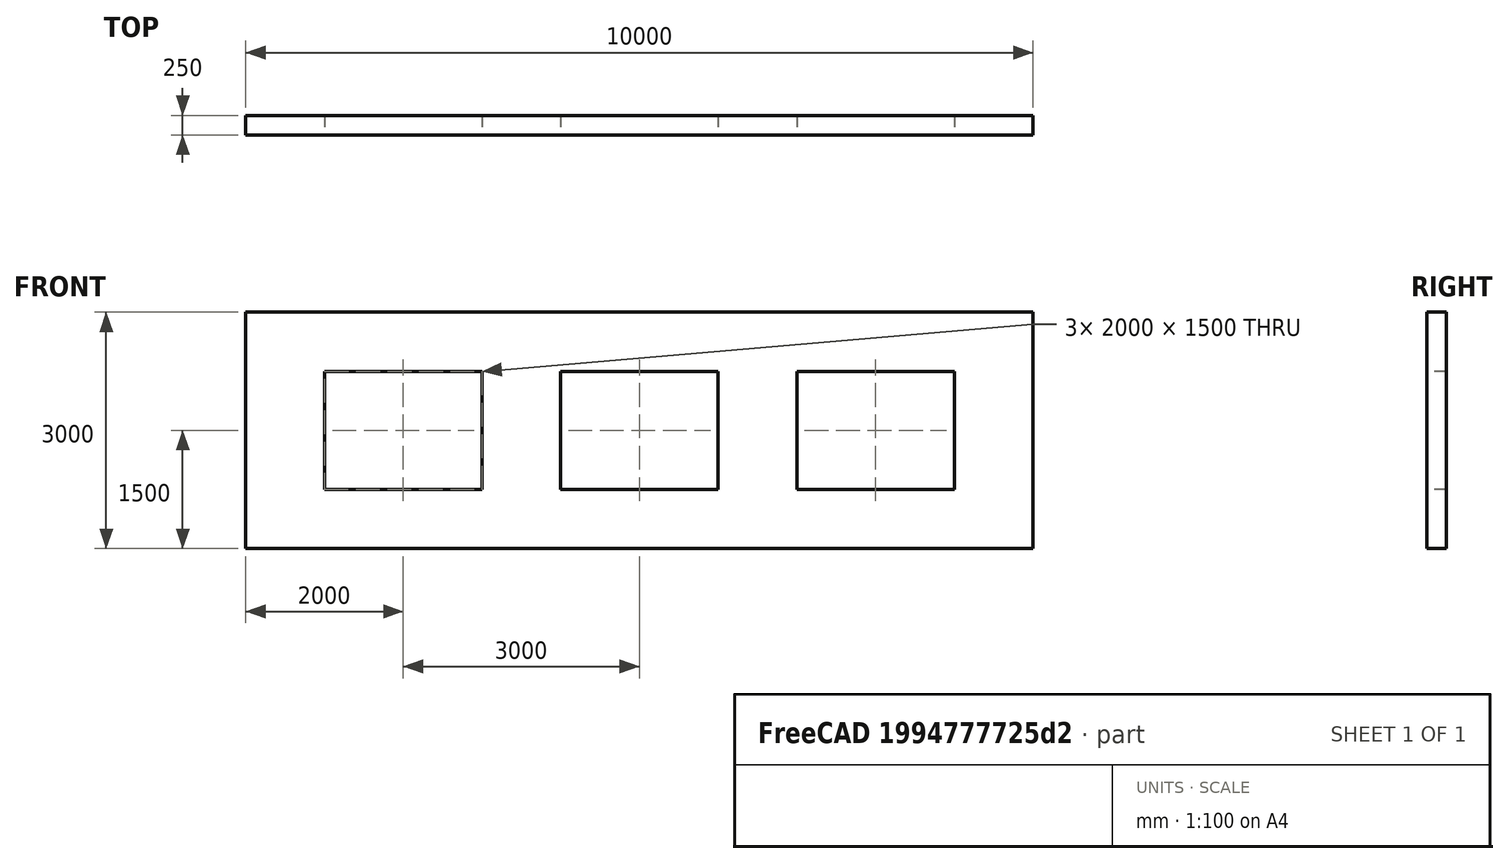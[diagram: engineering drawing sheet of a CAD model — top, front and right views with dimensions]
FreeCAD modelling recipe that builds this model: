
FCSTD DOCUMENT  (FreeCAD 0.21R33694 (Git))
Label: wall_with_openings
License: All rights reserved
LicenseURL: http://en.wikipedia.org/wiki/All_rights_reserved
objects: Part::Box×1, Sketcher::SketchObject×1, Part::Extrusion×1, Part::Cut×1, Fem::ConstraintFixed×1, App::MaterialObjectPython×1, Fem::ConstraintForce×1, Fem::FemSolverObjectPython×1, Fem::FemMeshObjectPython×1, Fem::FemAnalysis×1
note: 4 computed .brp shape members not serialized (recipe doc carries the construction recipe); baked Part::Feature solids carry a one-line shape summary decoded from their .brp

FEATURE [Part::Box] Box  label="Cube"
  AttacherType = Attacher::AttachEngine3D
  Height = 3000
  Length = 10000
  Width = 250
FEATURE [Sketcher::SketchObject] Sketch
  FullyConstrained = true
  MapMode = 5
  Placement = pos=(0,0,0) rot=(1,0,0;1.5708rad)
  Support = -> [Box]
  sketch-geometry (12):
    g0: LineSegment StartX=1000 StartY=750 StartZ=0 EndX=3000 EndY=750 EndZ=0
    g1: LineSegment StartX=3000 StartY=750 StartZ=0 EndX=3000 EndY=2250 EndZ=0
    g2: LineSegment StartX=3000 StartY=2250 StartZ=0 EndX=1000 EndY=2250 EndZ=0
    g3: LineSegment StartX=1000 StartY=2250 StartZ=0 EndX=1000 EndY=750 EndZ=0
    g4: LineSegment StartX=4000 StartY=750 StartZ=0 EndX=6000 EndY=750 EndZ=0
    g5: LineSegment StartX=6000 StartY=750 StartZ=0 EndX=6000 EndY=2250 EndZ=0
    g6: LineSegment StartX=6000 StartY=2250 StartZ=0 EndX=4000 EndY=2250 EndZ=0
    g7: LineSegment StartX=4000 StartY=2250 StartZ=0 EndX=4000 EndY=750 EndZ=0
    g8: LineSegment StartX=7000 StartY=750 StartZ=0 EndX=9000 EndY=750 EndZ=0
    g9: LineSegment StartX=9000 StartY=750 StartZ=0 EndX=9000 EndY=2250 EndZ=0
    g10: LineSegment StartX=9000 StartY=2250 StartZ=0 EndX=7000 EndY=2250 EndZ=0
    g11: LineSegment StartX=7000 StartY=2250 StartZ=0 EndX=7000 EndY=750 EndZ=0
  constraints (36):
    c: Coincident(g0,g1)
    c: Coincident(g1,g2)
    c: Coincident(g2,g3)
    c: Coincident(g3,g0)
    c: Horizontal(g0)
    c: Horizontal(g2)
    c: Vertical(g1)
    c: Vertical(g3)
    c: Coincident(g4,g5)
    c: Coincident(g5,g6)
    c: Coincident(g6,g7)
    c: Coincident(g7,g4)
    c: Horizontal(g4)
    c: Horizontal(g6)
    c: Vertical(g5)
    c: Vertical(g7)
    c: Coincident(g8,g9)
    c: Coincident(g9,g10)
    c: Coincident(g10,g11)
    c: Coincident(g11,g8)
    c: Horizontal(g8)
    c: Horizontal(g10)
    c: Vertical(g9)
    c: Vertical(g11)
    c: DistanceY(g3,g3) = 1500
    c: DistanceY(g7,g7) = 1500
    c: DistanceY(g11,g11) = 1500
    c: DistanceY(g-1,g0) = 750
    c: DistanceY(g-1,g4) = 750
    c: DistanceY(g-1,g8) = 750
    c: DistanceX(g0,g0) = 2000
    c: DistanceX(g4,g4) = 2000
    c: DistanceX(g8,g8) = 2000
    c: DistanceX(g1,g6) = 1000
    c: DistanceX(g5,g10) = 1000
    c: DistanceX(g-1,g0) = 1000
FEATURE [Part::Extrusion] Extrude
  Base = -> Sketch
  Dir = (0,-1,2e-16)
  DirMode = 2
  FaceMakerClass = Part::FaceMakerBullseye
  LengthFwd = 0
  LengthRev = 350
  Solid = true
  Symmetric = false
FEATURE [Part::Cut] Cut
  Base = -> Box
  Tool = -> Extrude
FEATURE [Fem::ConstraintFixed] ConstraintFixed
  NormalDirection = (-1,0,0)
  Normals = (72) [(-1,0,0),(-1,0,0),(-1,0,0),(-1,0,0),(-1,0,0),(-1,0,0),(-1,0,0),(-1,0,0),(-1,0,0),(-1,0,0),(-1,0,0),(-1,0,0),(-1,0,0),(-1,0,0),(-1,0,0),(-1,0,0),+56 more]
  Points = (72) [(0,250,0),(0,250,375),(0,250,750),(0,250,1125),(0,250,1500),(0,250,1875),(0,250,2250),(0,250,2625),(0,250,3000),(0,166.667,0),(0,166.667,375),+61 more]
  References = -> [Cut]
  Scale = 40
FEATURE [App::MaterialObjectPython] MaterialSolid  # material (typed FeaturePython)
  Category = 0
  Material = AuthorAndLicense=(c) 2013 Yorik van Havre (CC-BY 3.0),CardName=Concrete-Generic,CompressiveStrength=25 MPa,Density=2400 kg/m^3,+7 more (map truncated)
FEATURE [Fem::ConstraintForce] ConstraintForce
  DirectionVector = (0,0,-1)
  Force = 1000000
  NormalDirection = (0,0,1)
  Points = (68) [(0,0,3000),(625,0,3000),(1250,0,3000),(1875,0,3000),(2500,0,3000),(3125,0,3000),(3750,0,3000),(4375,0,3000),(5000,0,3000),(5625,0,3000),(6250,0,3000),+57 more]
  References = -> [Cut]
  Reversed = true
  Scale = 62
FEATURE [Fem::FemSolverObjectPython] SolverCcxTools  # FEM object (typed FeaturePython)
  AnalysisType = 0
  BeamShellResultOutput3D = false
  BucklingFactors = 1
  EigenmodeHighLimit = 1000000
  EigenmodeLowLimit = 0
  EigenmodesCount = 10
  GeometricalNonlinearity = 0
  IterationsControlParameterCutb = 0.25,0.5,0.75,0.85,,,1.5,
  IterationsControlParameterIter = 4,8,9,200,10,400,,200,,
  IterationsControlParameterTimeUse = false
  IterationsThermoMechMaximum = 2000
  IterationsUserDefinedIncrementations = false
  IterationsUserDefinedTimeStepLength = false
  MaterialNonlinearity = 0
  MatrixSolverType = 0
  SplitInputWriter = false
  ThermoMechSteadyState = true
  TimeEnd = 1
  TimeInitialStep = 0.01
FEATURE [Fem::FemMeshObjectPython] FEMMeshGmsh  # FEM object (typed FeaturePython)
  Algorithm2D = 0
  Algorithm3D = 0
  CharacteristicLengthMax = 250
  CharacteristicLengthMin = 0
  CoherenceMesh = true
  ElementDimension = 0
  ElementOrder = 1
  GeometryTolerance = 1e-06
  GroupsOfNodes = false
  HighOrderOptimize = 0
  MeshSizeFromCurvature = 12
  OptimizeNetgen = false
  OptimizeStd = true
  Part = -> Cut
  RecombinationAlgorithm = 0
  Recombine3DAll = false
  RecombineAll = false
  SecondOrderLinear = false
FEATURE [Fem::FemAnalysis] Analysis
  Group = -> [ConstraintFixed,MaterialSolid,ConstraintForce,SolverCcxTools,FEMMeshGmsh]
